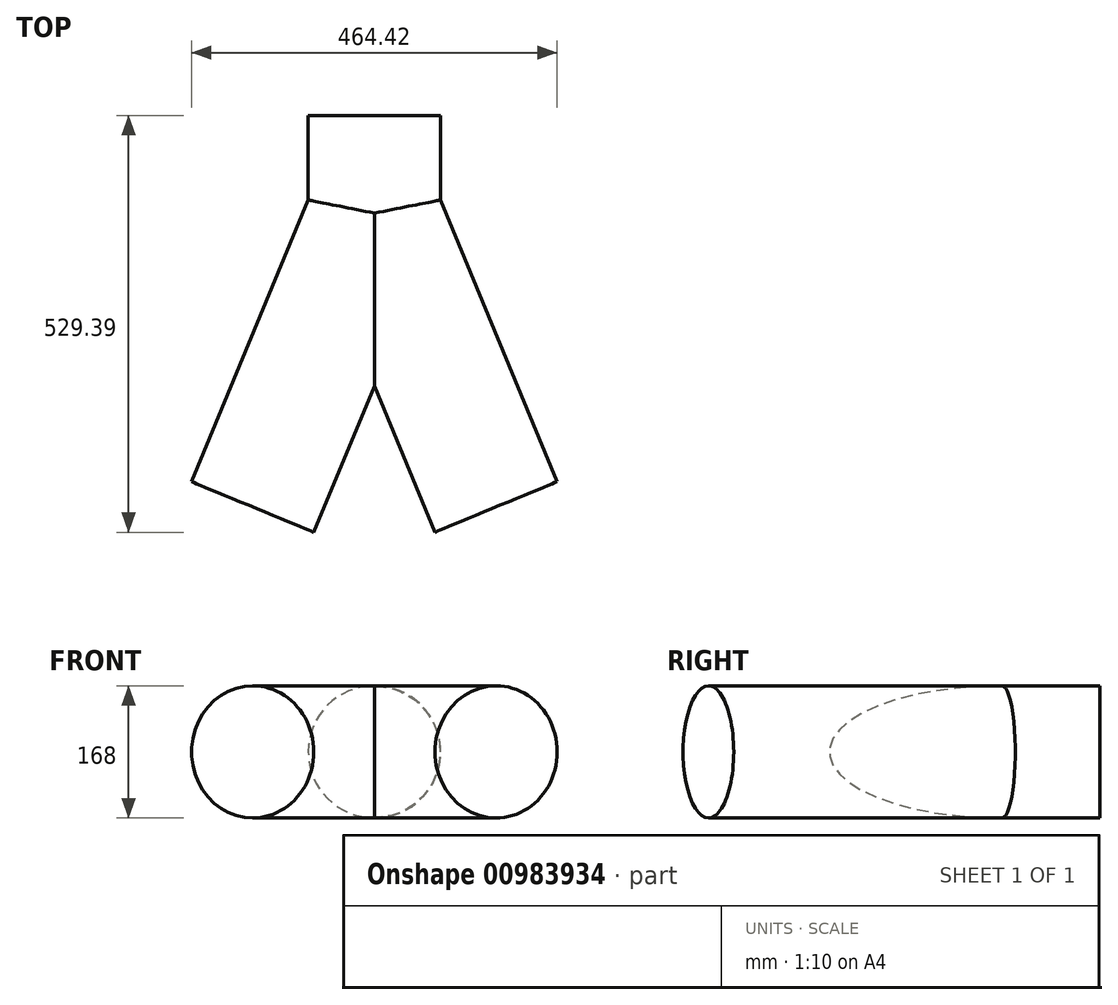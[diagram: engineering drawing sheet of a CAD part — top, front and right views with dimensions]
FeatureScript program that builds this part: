
annotation { "Feature Type Name" : "Feature", "Feature Type Description" : "" }
export const myFeature = defineFeature(function(context is Context, id is Id, definition is map)
    precondition{}
    {
        {
            var Q0;
            Q0=qCreatedBy(makeId("Top.planeOp"),FACE);
            var sketch = newSketch(context, id + "F0", { "sketchPlane" : qUnion([Q0])});
            skLineSegment(sketch, "E0", {"start": v(0, 0) * mm, "end": v(0, 124) * mm});
            skLineSegment(sketch, "E1", {"start": v(0, 0) * mm, "end": v(-154.6, -373.25) * mm});
            skLineSegment(sketch, "E2.MirrorCS", {"start": v(0, 0) * mm, "end": v(154.6, -373.25) * mm});
            skSolve(sketch);
        }
        {
            var Q0;
            Q0=qCreatedBy(makeId("Front.planeOp"),FACE);
            var sketch = newSketch(context, id + "F1", { "sketchPlane" : qUnion([Q0])});
            skCircle(sketch, "E3", {"center": v(0, 0) * mm, "radius": 84 * mm});
            skSolve(sketch);
        }
        {
            var Q0;
            Q0=makeQuery(id+"F1.imprint","IMPRINT",FACE,{"disambiguationData":[TD([[makeQuery(id+"F1.imprint","IMPRINT",EDGE,{"derivedFrom":sQuery(id+"F1.wireOp",EDGE,"E3")}),1.0]])]});
            var Q1;
            Q1=sQuery(id+"F0.wireOp",EDGE,"E0");
            sweep(context, id + "F2", {"profiles" : qUnion([Q0]), "path" : qUnion([Q1])});
        }
        {
            var Q0;
            Q0=sQuery(id+"F0.wireOp",EDGE,"E1");
            var Q1;
            Q1=sQuery(id+"F0.wireOp",VERTEX,"E1.end");
            cPlane(context, id + "F3", {"entities" : qUnion([Q0, Q1]), "cplaneType" : CPlaneType.LINE_POINT, "offset" : 25 * mm, "width" : 150 * mm, "height" : 150 * mm});
        }
        {
            var Q0;
            Q0=qCreatedBy(id+"F3.planeOp",FACE);
            var sketch = newSketch(context, id + "F4", { "sketchPlane" : qUnion([Q0])});
            skCircle(sketch, "E4", {"center": v(0, 0) * mm, "radius": 84 * mm});
            skSolve(sketch);
        }
        {
            var Q0;
            Q0=makeQuery(id+"F4.imprint","IMPRINT",FACE,{"disambiguationData":[TD([[makeQuery(id+"F4.imprint","IMPRINT",EDGE,{"derivedFrom":sQuery(id+"F4.wireOp",EDGE,"E4")}),1.0]])]});
            var Q1;
            Q1=sQuery(id+"F0.wireOp",EDGE,"E1");
            sweep(context, id + "F5", {"operationType" : NewBodyOperationType.ADD, "profiles" : qUnion([Q0]), "path" : qUnion([Q1])});
        }
        {
            var Q0;
            Q0=sQuery(id+"F0.wireOp",VERTEX,"E2.MirrorCS.end");
            var Q1;
            Q1=sQuery(id+"F0.wireOp",EDGE,"E2.MirrorCS");
            cPlane(context, id + "F6", {"entities" : qUnion([Q0, Q1]), "cplaneType" : CPlaneType.LINE_POINT, "offset" : 25 * mm, "width" : 150 * mm, "height" : 150 * mm});
        }
        {
            var Q0;
            Q0=qCreatedBy(id+"F6.planeOp",FACE);
            var sketch = newSketch(context, id + "F7", { "sketchPlane" : qUnion([Q0])});
            skCircle(sketch, "E5", {"center": v(0, 0) * mm, "radius": 84 * mm});
            skSolve(sketch);
        }
        {
            var Q0;
            Q0=makeQuery(id+"F7.imprint","IMPRINT",FACE,{"disambiguationData":[TD([[makeQuery(id+"F7.imprint","IMPRINT",EDGE,{"derivedFrom":sQuery(id+"F7.wireOp",EDGE,"E5")}),1.0]])]});
            var Q1;
            Q1=sQuery(id+"F0.wireOp",EDGE,"E2.MirrorCS");
            sweep(context, id + "F8", {"operationType" : NewBodyOperationType.ADD, "profiles" : qUnion([Q0]), "path" : qUnion([Q1])});
        }
    });
